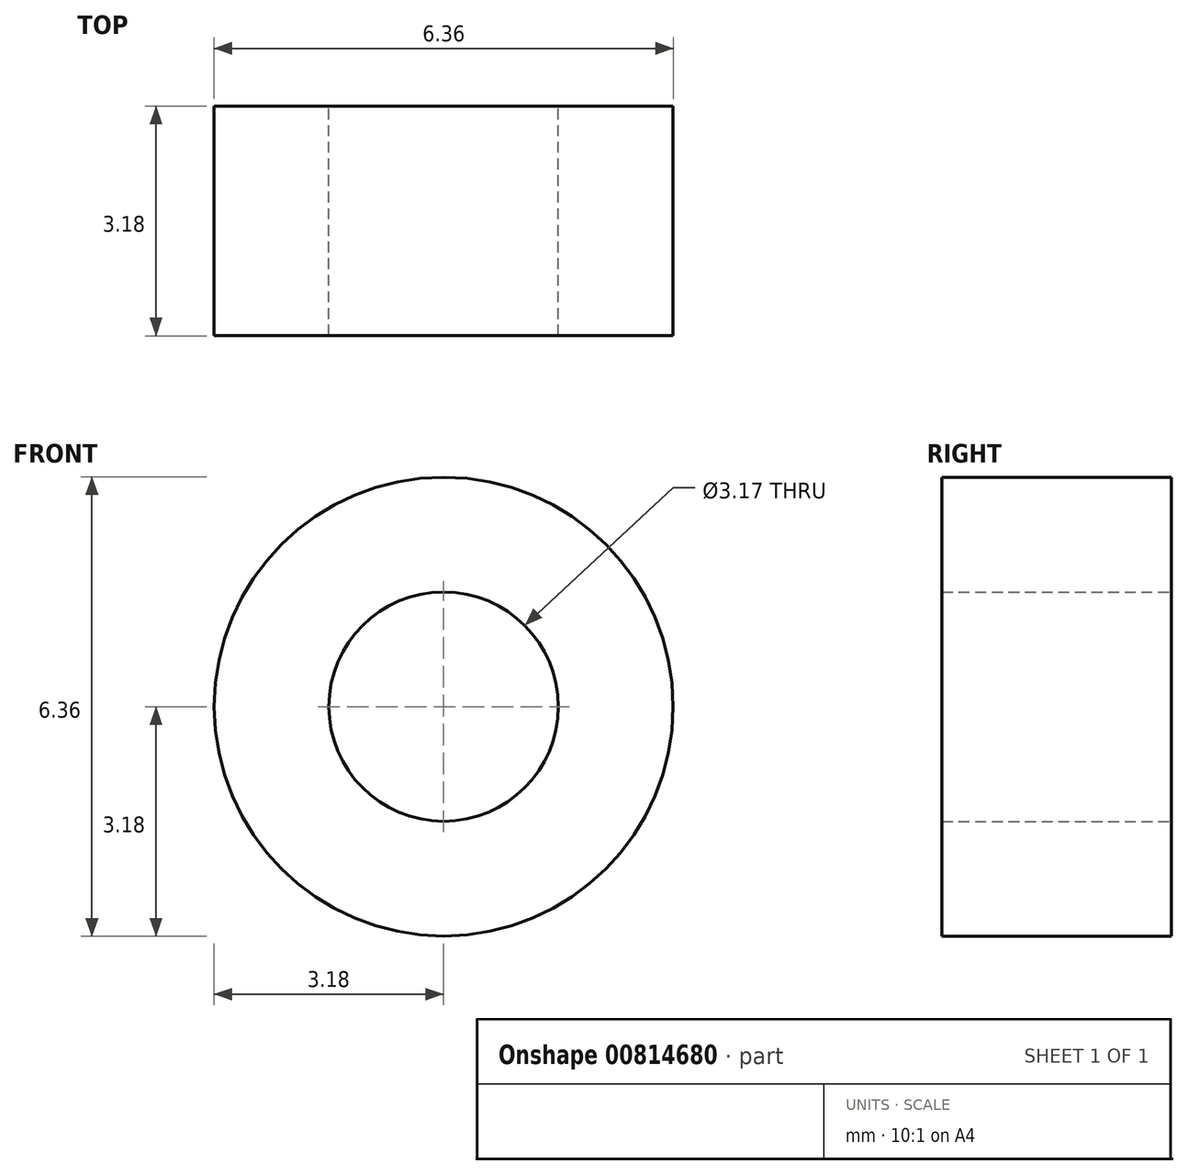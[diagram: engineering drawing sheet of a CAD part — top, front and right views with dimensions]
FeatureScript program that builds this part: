
annotation { "Feature Type Name" : "Feature", "Feature Type Description" : "" }
export const myFeature = defineFeature(function(context is Context, id is Id, definition is map)
    precondition{}
    {
        {
            var Q0;
            Q0=qCreatedBy(makeId("Front.planeOp"),FACE);
            var sketch = newSketch(context, id + "F0", { "sketchPlane" : qUnion([Q0])});
            skCircle(sketch, "E0", {"center": v(0, 0) * mm, "radius": 1.59 * mm});
            skCircle(sketch, "E1", {"center": v(0, 0) * mm, "radius": 3.18 * mm});
            skSolve(sketch);
        }
        {
            var Q0;
            Q0=makeQuery(id+"F0.imprint","IMPRINT",FACE,{"disambiguationData":[TD([[makeQuery(id+"F0.imprint","IMPRINT",EDGE,{"derivedFrom":sQuery(id+"F0.wireOp",EDGE,"E0")}),-1.0]])]});
            extrude(context, id + "F1", {"entities" : qUnion([Q0]), "depth" : 3.17 * mm, "offsetDistance" : 25.4 * mm});
        }
    });
